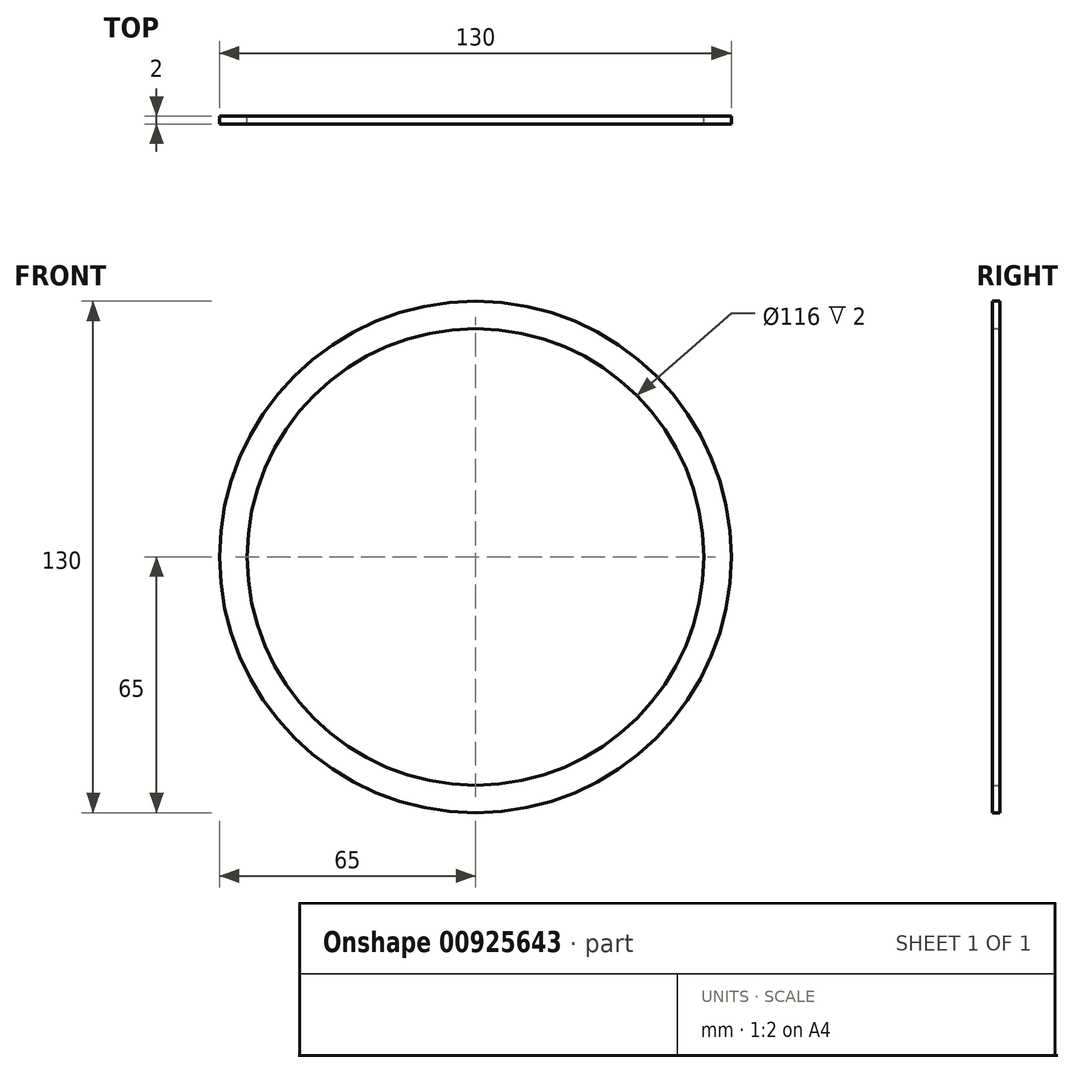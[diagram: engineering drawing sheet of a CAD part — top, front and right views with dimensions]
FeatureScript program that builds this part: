
annotation { "Feature Type Name" : "Feature", "Feature Type Description" : "" }
export const myFeature = defineFeature(function(context is Context, id is Id, definition is map)
    precondition{}
    {
        {
            var Q0;
            Q0=qCreatedBy(makeId("Front.planeOp"),FACE);
            var sketch = newSketch(context, id + "F0", { "sketchPlane" : qUnion([Q0])});
            skCircle(sketch, "E0", {"center": v(0, 0) * mm, "radius": 65 * mm});
            skCircle(sketch, "E1", {"center": v(0, 0) * mm, "radius": 58 * mm});
            skSolve(sketch);
        }
        {
            var Q0;
            Q0=makeQuery(id+"F0.imprint","IMPRINT",FACE,{"disambiguationData":[TD([[makeQuery(id+"F0.imprint","IMPRINT",EDGE,{"derivedFrom":sQuery(id+"F0.wireOp",EDGE,"E0")}),1.0]])]});
            extrude(context, id + "F1", {"entities" : qUnion([Q0]), "depth" : 2 * mm, "offsetDistance" : 25 * mm});
        }
    });
